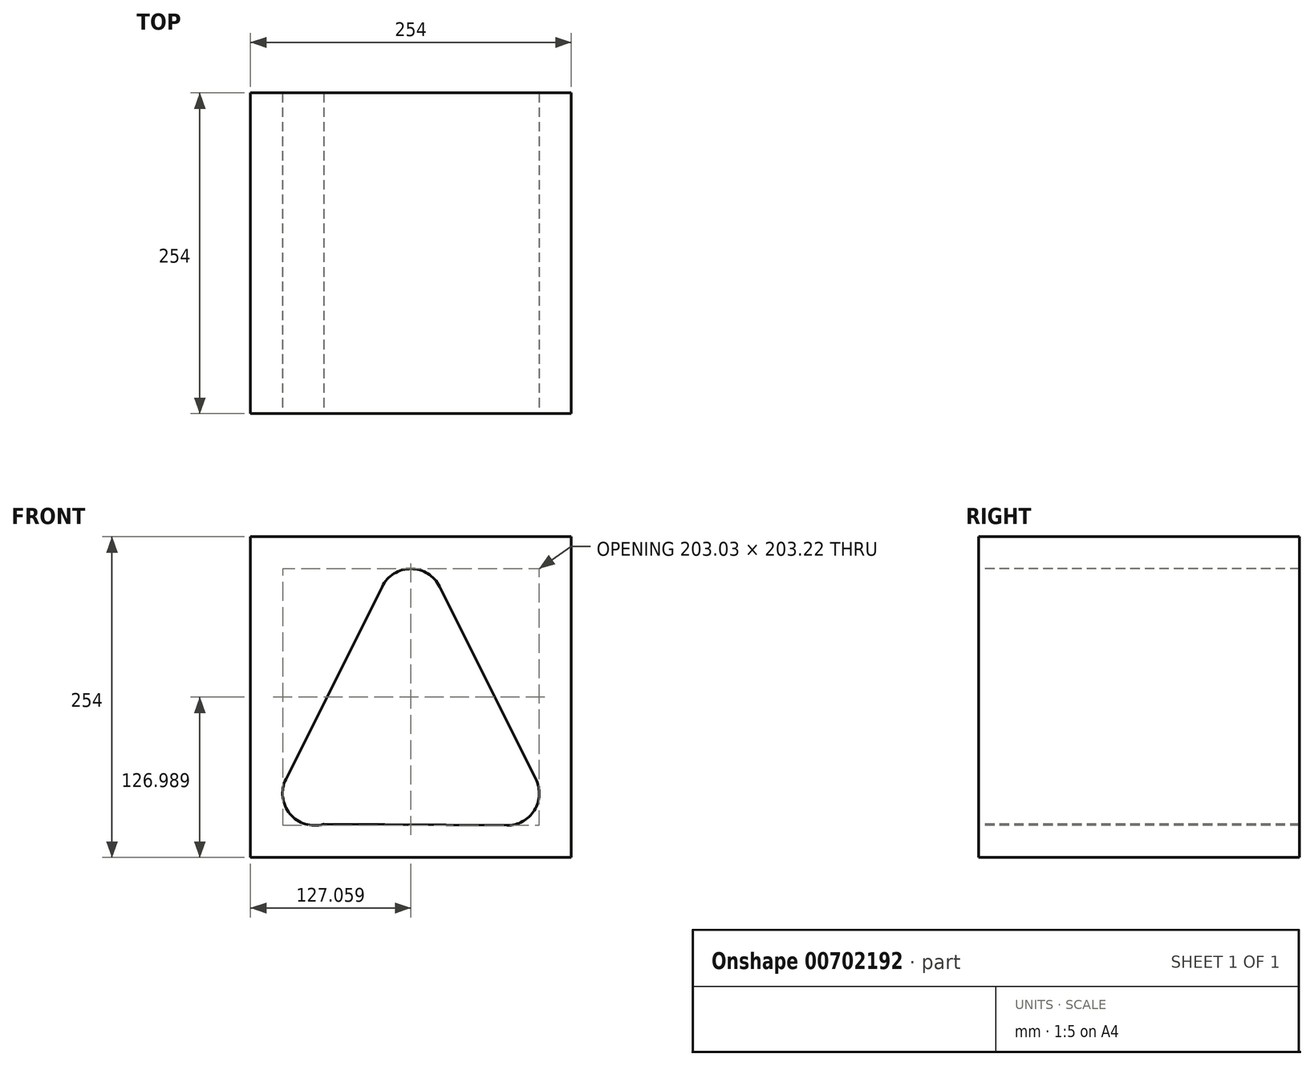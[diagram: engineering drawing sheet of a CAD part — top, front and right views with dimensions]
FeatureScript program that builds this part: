
annotation { "Feature Type Name" : "Feature", "Feature Type Description" : "" }
export const myFeature = defineFeature(function(context is Context, id is Id, definition is map)
    precondition{}
    {
        {
            var Q0;
            Q0=qCreatedBy(makeId("Front.planeOp"),FACE);
            var sketch = newSketch(context, id + "F0", { "sketchPlane" : qUnion([Q0])});
            skLineSegment(sketch, "E0", {"start": v(0, 0) * mm, "end": v(254, 0) * mm});
            skLineSegment(sketch, "E1", {"start": v(254, 0) * mm, "end": v(254, 254) * mm});
            skLineSegment(sketch, "E2", {"start": v(254, 254) * mm, "end": v(0, 254) * mm});
            skLineSegment(sketch, "E3", {"start": v(0, 254) * mm, "end": v(0, 0) * mm});
            skArc(sketch, "E4", {"start": v(28.06, 62.17) * mm, "mid": v(31.27, 34.53) * mm, "end": v(57.88, 26.38) * mm});
            skArc(sketch, "E5", {"start": v(203.03, 25.4) * mm, "mid": v(224.76, 37.37) * mm, "end": v(225.92, 62.16) * mm});
            skArc(sketch, "E6", {"start": v(149.72, 214.56) * mm, "mid": v(127, 228.6) * mm, "end": v(104.28, 214.56) * mm});
            skLineSegment(sketch, "E7", {"start": v(149.72, 214.56) * mm, "end": v(225.92, 62.16) * mm});
            skLineSegment(sketch, "E8", {"start": v(104.28, 214.56) * mm, "end": v(28.06, 62.17) * mm});
            skLineSegment(sketch, "E9", {"start": v(57.88, 26.38) * mm, "end": v(203.03, 25.4) * mm});
            skSolve(sketch);
        }
        {
            var Q0;
            Q0=makeQuery(id+"F0.imprint","IMPRINT",FACE,{"disambiguationData":[TD([[makeQuery(id+"F0.imprint","IMPRINT",EDGE,{"derivedFrom":sQuery(id+"F0.wireOp",EDGE,"E0")}),1.0]])]});
            extrude(context, id + "F1", {"entities" : qUnion([Q0]), "oppositeDirection" : true, "depth" : 254 * mm, "offsetDistance" : 25.4 * mm});
        }
    });
